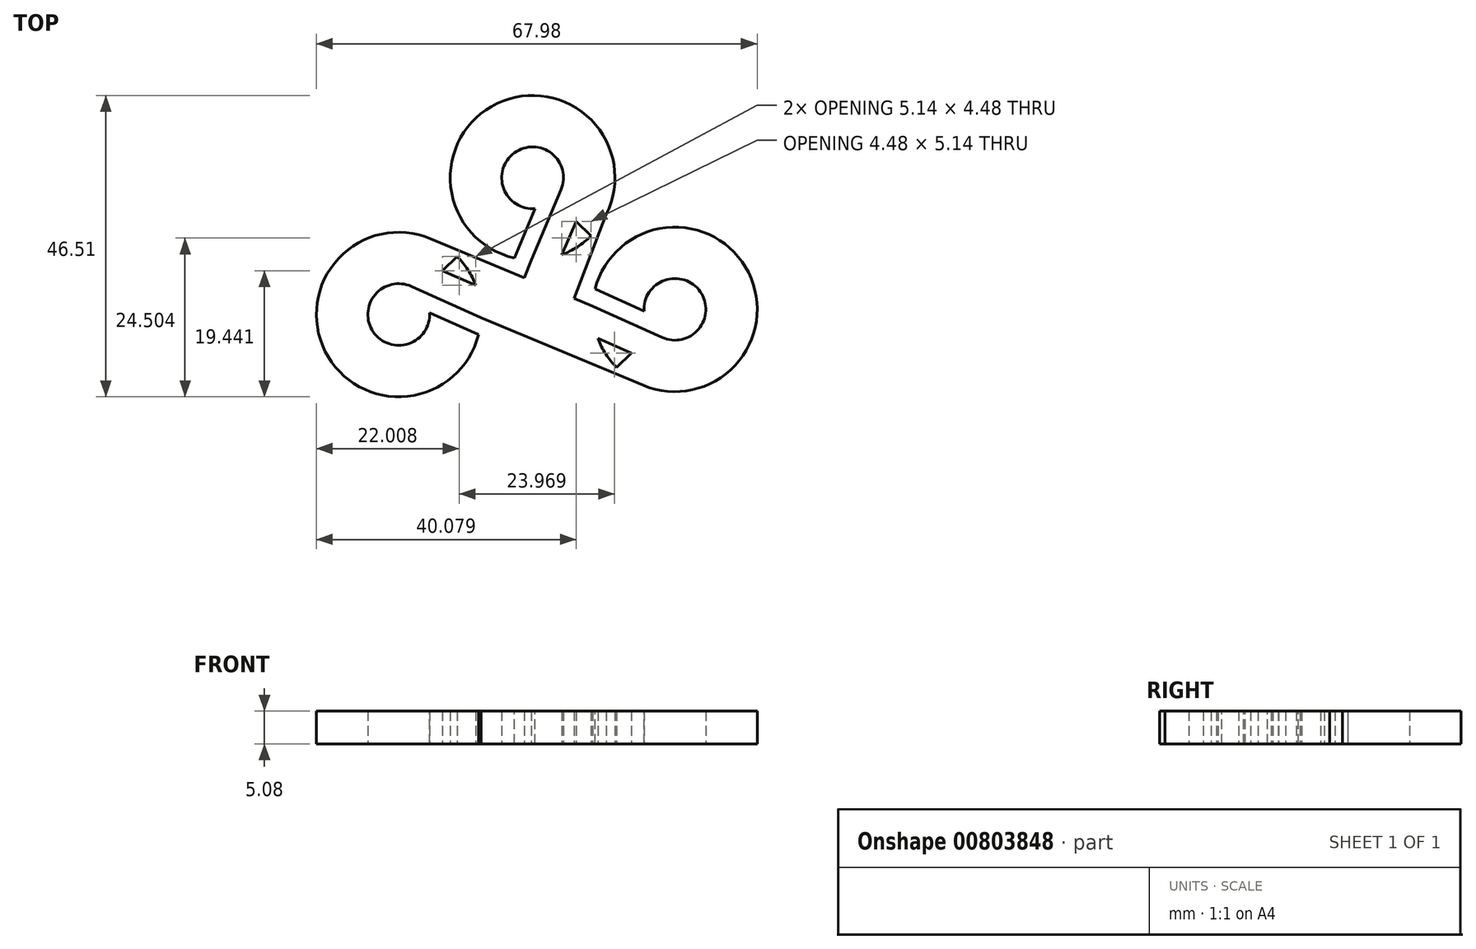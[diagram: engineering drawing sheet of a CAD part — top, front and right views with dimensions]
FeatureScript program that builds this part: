
annotation { "Feature Type Name" : "Feature", "Feature Type Description" : "" }
export const myFeature = defineFeature(function(context is Context, id is Id, definition is map)
    precondition{}
    {
        {
            var Q0;
            Q0=qCreatedBy(makeId("Top.planeOp"),FACE);
            var sketch = newSketch(context, id + "F0", { "sketchPlane" : qUnion([Q0])});
            skCircle(sketch, "E0", {"center": v(0, 0) * mm, "radius": 12.7 * mm});
            skCircle(sketch, "E1", {"center": v(21.94, -20.3) * mm, "radius": 12.7 * mm});
            skCircle(sketch, "E2", {"center": v(-20.64, -21.1) * mm, "radius": 12.7 * mm});
            skLineSegment(sketch, "E3", {"start": v(21.94, -20.3) * mm, "end": v(21.94, -33) * mm});
            skLineSegment(sketch, "E4", {"start": v(0, 0) * mm, "end": v(0, -12.7) * mm});
            skLineSegment(sketch, "E5", {"start": v(0, 0) * mm, "end": v(8.98, -8.98) * mm});
            skLineSegment(sketch, "E6", {"start": v(21.94, -20.3) * mm, "end": v(12.96, -29.29) * mm});
            skCircle(sketch, "E7", {"center": v(21.94, -20.3) * mm, "radius": 4.76 * mm});
            skLineSegment(sketch, "E8", {"start": v(21.94, -20.3) * mm, "end": v(17.45, -24.8) * mm});
            skCircle(sketch, "E9", {"center": v(0, 0) * mm, "radius": 4.76 * mm});
            skLineSegment(sketch, "E10", {"start": v(0, 0) * mm, "end": v(4.5, -4.5) * mm});
            skLineSegment(sketch, "E11", {"start": v(-20.64, -21.1) * mm, "end": v(-11.66, -12.13) * mm});
            skCircle(sketch, "E12", {"center": v(-20.64, -21.1) * mm, "radius": 4.76 * mm});
            skLineSegment(sketch, "E13", {"start": v(-20.64, -21.1) * mm, "end": v(-7.94, -21.1) * mm});
            skLineSegment(sketch, "E14", {"start": v(17.45, -24.8) * mm, "end": v(12.96, -29.29) * mm});
            skLineSegment(sketch, "E15", {"start": v(12.96, -29.29) * mm, "end": v(15.2, -27.04) * mm});
            skLineSegment(sketch, "E16", {"start": v(4.5, -4.5) * mm, "end": v(8.98, -8.98) * mm});
            skLineSegment(sketch, "E17", {"start": v(-16.15, -16.62) * mm, "end": v(-11.66, -12.13) * mm});
            skLineSegment(sketch, "E18", {"start": v(-17.27, -17.74) * mm, "end": v(17.06, -32.03) * mm});
            skLineSegment(sketch, "E19", {"start": v(18.58, -23.68) * mm, "end": v(-15.76, -9.38) * mm});
            skLineSegment(sketch, "E20", {"start": v(3.37, -3.37) * mm, "end": v(-1.24, -15.43) * mm});
            skLineSegment(sketch, "E21", {"start": v(-17.27, -17.74) * mm, "end": v(-13.9, -14.37) * mm});
            skLineSegment(sketch, "E22", {"start": v(-13.9, -14.37) * mm, "end": v(15.2, -27.04) * mm});
            skLineSegment(sketch, "E23", {"start": v(6.74, -6.74) * mm, "end": v(0.65, -20.7) * mm});
            skLineSegment(sketch, "E24", {"start": v(11.39, -5.62) * mm, "end": v(6.42, -18.62) * mm});
            skSolve(sketch);
        }
        {
            var Q0;
            Q0=qSketchRegion(id+"F0",true);
            var Q1;
            {var subQ0=sQuery(id+"F0.wireOp",EDGE,"yDXB3k3o-TFvE-FYoA-wN1f-QkH4QK7AQUMg");var subQ1=sQuery(id+"F0.wireOp",EDGE,"E0");var subQ2=makeQuery(id+"F0.imprint","INTERSECT",VERTEX,{"derivedFrom":[subQ1,subQ0]});Q1=makeQuery(id+"F0.imprint","IMPRINT",FACE,{"disambiguationData":[TD([[makeQuery(id+"F0.imprint","IMPRINT",EDGE,{"disambiguationData":[TD([[subQ2,-1.0]])],"derivedFrom":subQ1}),1.0]])]});}
            var Q2;
            {var subQ0=sQuery(id+"F0.wireOp",EDGE,"E17");var subQ3=sQuery(id+"F0.wireOp",EDGE,"J90078Zz-WnI3-3mMf-xPuW-VheWCmXxd4jc");var subQ5=makeQuery(id+"F0.imprint","INTERSECT",VERTEX,{"derivedFrom":[subQ0,subQ3]});Q2=makeQuery(id+"F0.imprint","IMPRINT",FACE,{"disambiguationData":[TD([[makeQuery(id+"F0.imprint","IMPRINT",EDGE,{"disambiguationData":[TD([[subQ5,-1.0]])],"derivedFrom":subQ3}),1.0]])]});}
            var Q3;
            {var subQ0=sQuery(id+"F0.wireOp",EDGE,"E16");var subQ3=sQuery(id+"F0.wireOp",EDGE,"qBhyJChg-6HFi-ImKc-3mO0-xAAPeeJnZw3U");var subQ5=makeQuery(id+"F0.imprint","INTERSECT",VERTEX,{"derivedFrom":[subQ0,subQ3]});Q3=makeQuery(id+"F0.imprint","IMPRINT",FACE,{"disambiguationData":[TD([[makeQuery(id+"F0.imprint","IMPRINT",EDGE,{"disambiguationData":[TD([[subQ5,-1.0]])],"derivedFrom":subQ3}),1.0]])]});}
            var Q4;
            {var subQ0=sQuery(id+"F0.wireOp",EDGE,"E15");Q4=makeQuery(id+"F0.imprint","IMPRINT",FACE,{"disambiguationData":[TD([[makeQuery(id+"F0.imprint","IMPRINT",EDGE,{"derivedFrom":subQ0}),1.0]])]});}
            var Q5;
            {var subQ0=sQuery(id+"F0.wireOp",EDGE,"uzKKBWqX-qUkN-Bwqt-uPOb-Zz89Ibqqk1gW");var subQ1=sQuery(id+"F0.wireOp",EDGE,"E2");var subQ2=makeQuery(id+"F0.imprint","INTERSECT",VERTEX,{"derivedFrom":[subQ1,subQ0]});Q5=makeQuery(id+"F0.imprint","IMPRINT",FACE,{"disambiguationData":[TD([[makeQuery(id+"F0.imprint","IMPRINT",EDGE,{"disambiguationData":[TD([[subQ2,-1.0]])],"derivedFrom":subQ1}),-1.0]])]});}
            var Q6;
            {var subQ0=sQuery(id+"F0.wireOp",EDGE,"bYxaBZOP-HbRW-pdFW-15Ub-mmeAeTIA2QFz");Q6=makeQuery(id+"F0.imprint","IMPRINT",FACE,{"disambiguationData":[TD([[makeQuery(id+"F0.imprint","IMPRINT",EDGE,{"derivedFrom":subQ0}),-1.0]])]});}
            var Q7;
            {var subQ0=sQuery(id+"F0.wireOp",EDGE,"uzKKBWqX-qUkN-Bwqt-uPOb-Zz89Ibqqk1gW");var subQ1=sQuery(id+"F0.wireOp",EDGE,"E2");var subQ2=makeQuery(id+"F0.imprint","INTERSECT",VERTEX,{"derivedFrom":[subQ1,subQ0]});Q7=makeQuery(id+"F0.imprint","IMPRINT",FACE,{"disambiguationData":[TD([[makeQuery(id+"F0.imprint","IMPRINT",EDGE,{"disambiguationData":[TD([[subQ2,-1.0]])],"derivedFrom":subQ1}),1.0]])]});}
            var Q8;
            {var subQ0=sQuery(id+"F0.wireOp",EDGE,"Z3ejKgqz-Hqn6-uIZ8-Rk3e-6zc6qRlB8dJ0");Q8=makeQuery(id+"F0.imprint","IMPRINT",FACE,{"disambiguationData":[TD([[makeQuery(id+"F0.imprint","IMPRINT",EDGE,{"derivedFrom":subQ0}),-1.0]])]});}
            var Q9;
            {var subQ1=sQuery(id+"F0.wireOp",EDGE,"E0");var subQ3=sQuery(id+"F0.wireOp",EDGE,"qBhyJChg-6HFi-ImKc-3mO0-xAAPeeJnZw3U");var subQ4=makeQuery(id+"F0.imprint","INTERSECT",VERTEX,{"derivedFrom":[subQ1,subQ3]});Q9=makeQuery(id+"F0.imprint","IMPRINT",FACE,{"disambiguationData":[TD([[makeQuery(id+"F0.imprint","IMPRINT",EDGE,{"disambiguationData":[TD([[subQ4,-1.0]])],"derivedFrom":subQ3}),1.0]])]});}
            var Q10;
            {var subQ3=sQuery(id+"F0.wireOp",EDGE,"E0");var subQ5=sQuery(id+"F0.wireOp",EDGE,"E4");var subQ6=makeQuery(id+"F0.imprint","INTERSECT",VERTEX,{"derivedFrom":[subQ3,subQ5]});Q10=makeQuery(id+"F0.imprint","IMPRINT",FACE,{"disambiguationData":[TD([[makeQuery(id+"F0.imprint","IMPRINT",EDGE,{"disambiguationData":[TD([[subQ6,-1.0]])],"derivedFrom":subQ3}),1.0]])]});}
            var Q11;
            {var subQ0=sQuery(id+"F0.wireOp",EDGE,"yDXB3k3o-TFvE-FYoA-wN1f-QkH4QK7AQUMg");var subQ1=sQuery(id+"F0.wireOp",EDGE,"E0");var subQ2=makeQuery(id+"F0.imprint","INTERSECT",VERTEX,{"derivedFrom":[subQ1,subQ0]});Q11=makeQuery(id+"F0.imprint","IMPRINT",FACE,{"disambiguationData":[TD([[makeQuery(id+"F0.imprint","IMPRINT",EDGE,{"disambiguationData":[TD([[subQ2,-1.0]])],"derivedFrom":subQ1}),-1.0]])]});}
            var Q12;
            {var subQ0=sQuery(id+"F0.wireOp",EDGE,"Z3ejKgqz-Hqn6-uIZ8-Rk3e-6zc6qRlB8dJ0");Q12=makeQuery(id+"F0.imprint","IMPRINT",FACE,{"disambiguationData":[TD([[makeQuery(id+"F0.imprint","IMPRINT",EDGE,{"derivedFrom":subQ0}),1.0]])]});}
            var Q13;
            {var subQ0=sQuery(id+"F0.wireOp",EDGE,"6yfvUeka-AtBQ-0gim-mu1m-la48lc1LBtnG");var subQ5=sQuery(id+"F0.wireOp",EDGE,"qBhyJChg-6HFi-ImKc-3mO0-xAAPeeJnZw3U");var subQ6=makeQuery(id+"F0.imprint","INTERSECT",VERTEX,{"derivedFrom":[subQ0,subQ5]});Q13=makeQuery(id+"F0.imprint","IMPRINT",FACE,{"disambiguationData":[TD([[makeQuery(id+"F0.imprint","IMPRINT",EDGE,{"disambiguationData":[TD([[subQ6,1.0]])],"derivedFrom":subQ5}),-1.0]])]});}
            var Q14;
            {var subQ0=sQuery(id+"F0.wireOp",EDGE,"6yfvUeka-AtBQ-0gim-mu1m-la48lc1LBtnG");var subQ5=sQuery(id+"F0.wireOp",EDGE,"qBhyJChg-6HFi-ImKc-3mO0-xAAPeeJnZw3U");var subQ6=makeQuery(id+"F0.imprint","INTERSECT",VERTEX,{"derivedFrom":[subQ0,subQ5]});Q14=makeQuery(id+"F0.imprint","IMPRINT",FACE,{"disambiguationData":[TD([[makeQuery(id+"F0.imprint","IMPRINT",EDGE,{"disambiguationData":[TD([[subQ6,1.0]])],"derivedFrom":subQ5}),1.0]])]});}
            var Q15;
            {var subQ0=sQuery(id+"F0.wireOp",EDGE,"z5MUbxWM-Vo3r-AQEv-g91w-RWlkdqbgf4P1");Q15=makeQuery(id+"F0.imprint","IMPRINT",FACE,{"disambiguationData":[TD([[makeQuery(id+"F0.imprint","IMPRINT",EDGE,{"derivedFrom":subQ0}),-1.0]])]});}
            var Q16;
            {var subQ1=sQuery(id+"F0.wireOp",EDGE,"E12");var subQ3=sQuery(id+"F0.wireOp",EDGE,"E13");var subQ4=makeQuery(id+"F0.imprint","INTERSECT",VERTEX,{"derivedFrom":[subQ1,subQ3]});Q16=makeQuery(id+"F0.imprint","IMPRINT",FACE,{"disambiguationData":[TD([[makeQuery(id+"F0.imprint","IMPRINT",EDGE,{"disambiguationData":[TD([[subQ4,-1.0]])],"derivedFrom":subQ3}),1.0]])]});}
            var Q17;
            {var subQ3=sQuery(id+"F0.wireOp",EDGE,"E2");var subQ7=sQuery(id+"F0.wireOp",EDGE,"E13");var subQ8=makeQuery(id+"F0.imprint","INTERSECT",VERTEX,{"derivedFrom":[subQ3,subQ7]});Q17=makeQuery(id+"F0.imprint","IMPRINT",FACE,{"disambiguationData":[TD([[makeQuery(id+"F0.imprint","IMPRINT",EDGE,{"disambiguationData":[TD([[subQ8,-1.0]])],"derivedFrom":subQ3}),1.0]])]});}
            var Q18;
            {var subQ5=sQuery(id+"F0.wireOp",EDGE,"E14");Q18=makeQuery(id+"F0.imprint","IMPRINT",FACE,{"disambiguationData":[TD([[makeQuery(id+"F0.imprint","IMPRINT",EDGE,{"derivedFrom":subQ5}),-1.0]])]});}
            var Q19;
            {var subQ0=sQuery(id+"F0.wireOp",EDGE,"NG6Fn4Pl-cfwn-nJXz-Nv7R-ltP6G86gKaW2");var subQ1=sQuery(id+"F0.wireOp",EDGE,"E1");var subQ2=makeQuery(id+"F0.imprint","INTERSECT",VERTEX,{"derivedFrom":[subQ1,subQ0]});Q19=makeQuery(id+"F0.imprint","IMPRINT",FACE,{"disambiguationData":[TD([[makeQuery(id+"F0.imprint","IMPRINT",EDGE,{"disambiguationData":[TD([[subQ2,-1.0]])],"derivedFrom":subQ1}),-1.0]])]});}
            var Q20;
            {var subQ0=sQuery(id+"F0.wireOp",EDGE,"bYxaBZOP-HbRW-pdFW-15Ub-mmeAeTIA2QFz");Q20=makeQuery(id+"F0.imprint","IMPRINT",FACE,{"disambiguationData":[TD([[makeQuery(id+"F0.imprint","IMPRINT",EDGE,{"derivedFrom":subQ0}),1.0]])]});}
            var Q21;
            {var subQ1=sQuery(id+"F0.wireOp",EDGE,"z5MUbxWM-Vo3r-AQEv-g91w-RWlkdqbgf4P1");Q21=makeQuery(id+"F0.imprint","IMPRINT",FACE,{"disambiguationData":[TD([[makeQuery(id+"F0.imprint","IMPRINT",EDGE,{"derivedFrom":subQ1}),1.0]])]});}
            var Q22;
            {var subQ0=sQuery(id+"F0.wireOp",EDGE,"eJoCJf4v-nHHx-lm19-L27D-6VjAbPNY3byg");var subQ1=sQuery(id+"F0.wireOp",EDGE,"E2");var subQ2=makeQuery(id+"F0.imprint","INTERSECT",VERTEX,{"derivedFrom":[subQ1,subQ0]});Q22=makeQuery(id+"F0.imprint","IMPRINT",FACE,{"disambiguationData":[TD([[makeQuery(id+"F0.imprint","IMPRINT",EDGE,{"disambiguationData":[TD([[subQ2,-1.0]])],"derivedFrom":subQ1}),1.0]])]});}
            var Q23;
            {var subQ0=sQuery(id+"F0.wireOp",EDGE,"E9");var subQ1=sQuery(id+"F0.wireOp",EDGE,"E4");var subQ2=makeQuery(id+"F0.imprint","INTERSECT",VERTEX,{"derivedFrom":[subQ1,subQ0]});Q23=makeQuery(id+"F0.imprint","IMPRINT",FACE,{"disambiguationData":[TD([[makeQuery(id+"F0.imprint","IMPRINT",EDGE,{"disambiguationData":[TD([[subQ2,-1.0]])],"derivedFrom":subQ1}),1.0]])]});}
            var Q24;
            {var subQ0=sQuery(id+"F0.wireOp",EDGE,"E17");Q24=makeQuery(id+"F0.imprint","IMPRINT",FACE,{"disambiguationData":[TD([[makeQuery(id+"F0.imprint","IMPRINT",EDGE,{"derivedFrom":subQ0}),-1.0]])]});}
            var Q25;
            {var subQ0=sQuery(id+"F0.wireOp",EDGE,"E16");var subQ1=sQuery(id+"F0.wireOp",EDGE,"E0");var subQ2=makeQuery(id+"F0.imprint","INTERSECT",VERTEX,{"derivedFrom":[subQ1,subQ0]});Q25=makeQuery(id+"F0.imprint","IMPRINT",FACE,{"disambiguationData":[TD([[makeQuery(id+"F0.imprint","IMPRINT",EDGE,{"disambiguationData":[TD([[subQ2,1.0]])],"derivedFrom":subQ1}),1.0]])]});}
            extrude(context, id + "F1", {"entities" : qUnion([Q0, Q1, Q2, Q3, Q4, Q5, Q6, Q7, Q8, Q9, Q10, Q11, Q12, Q13, Q14, Q15, Q16, Q17, Q18, Q19, Q20, Q21, Q22, Q23, Q24, Q25]), "depth" : 5.08 * mm, "offsetDistance" : 25.4 * mm});
        }
        {
            var Q0;
            Q0=makeQuery(id+"F1.opExtrude","CAP_FACE",FACE,{"disambiguationData":[OSD([sQuery(id+"F0.wireOp",EDGE,"E0"),sQuery(id+"F0.wireOp",EDGE,"E1"),sQuery(id+"F0.wireOp",EDGE,"E2"),sQuery(id+"F0.wireOp",EDGE,"VeAweMac-LZ9O-rFIa-PTyz-U5xl3IZNd5pn"),sQuery(id+"F0.wireOp",EDGE,"E7"),sQuery(id+"F0.wireOp",EDGE,"NG6Fn4Pl-cfwn-nJXz-Nv7R-ltP6G86gKaW2"),sQuery(id+"F0.wireOp",EDGE,"E9"),sQuery(id+"F0.wireOp",EDGE,"yDXB3k3o-TFvE-FYoA-wN1f-QkH4QK7AQUMg"),sQuery(id+"F0.wireOp",EDGE,"6yfvUeka-AtBQ-0gim-mu1m-la48lc1LBtnG"),sQuery(id+"F0.wireOp",EDGE,"E12"),sQuery(id+"F0.wireOp",EDGE,"uzKKBWqX-qUkN-Bwqt-uPOb-Zz89Ibqqk1gW"),sQuery(id+"F0.wireOp",EDGE,"z5MUbxWM-Vo3r-AQEv-g91w-RWlkdqbgf4P1"),sQuery(id+"F0.wireOp",EDGE,"qBhyJChg-6HFi-ImKc-3mO0-xAAPeeJnZw3U"),sQuery(id+"F0.wireOp",EDGE,"Vy6klFHD-ql6F-NG0b-UYJ5-acndccB01QWS"),sQuery(id+"F0.wireOp",EDGE,"OdPr5M7K-QP7o-Xsb9-YXNN-OMWYOfSv6xGX"),sQuery(id+"F0.wireOp",EDGE,"tfzjCEgK-RNZ7-z4IH-43NG-UBwa0SwhfyJe")])],"isStart":false});
            var sketch = newSketch(context, id + "F2", { "sketchPlane" : qUnion([Q0])});
            skLineSegment(sketch, "E25", {"start": v(-0.2, -12.7) * mm, "end": v(4.39, -1.86) * mm});
            skLineSegment(sketch, "E26", {"start": v(-2.82, -12.38) * mm, "end": v(0.4, -4.75) * mm});
            skLineSegment(sketch, "E27", {"start": v(-7.95, -21.62) * mm, "end": v(-18.68, -16.77) * mm});
            skLineSegment(sketch, "E28", {"start": v(-15.88, -20.82) * mm, "end": v(-8.33, -24.24) * mm});
            skLineSegment(sketch, "E29", {"start": v(9.25, -19.8) * mm, "end": v(19.98, -24.65) * mm});
            skLineSegment(sketch, "E30", {"start": v(9.63, -17.18) * mm, "end": v(17.19, -20.6) * mm});
            skSolve(sketch);
        }
        {
            var Q0;
            {var subQ0=sQuery(id+"F2.wireOp",EDGE,"E27");Q0=makeQuery(id+"F2.imprint","IMPRINT",FACE,{"disambiguationData":[TD([[makeQuery(id+"F2.imprint","IMPRINT",EDGE,{"derivedFrom":subQ0}),1.0]])]});}
            var Q1;
            {var subQ0=sQuery(id+"F2.wireOp",EDGE,"E25");Q1=makeQuery(id+"F2.imprint","IMPRINT",FACE,{"disambiguationData":[TD([[makeQuery(id+"F2.imprint","IMPRINT",EDGE,{"derivedFrom":subQ0}),1.0]])]});}
            var Q2;
            {var subQ0=sQuery(id+"F2.wireOp",EDGE,"E29");Q2=makeQuery(id+"F2.imprint","IMPRINT",FACE,{"disambiguationData":[TD([[makeQuery(id+"F2.imprint","IMPRINT",EDGE,{"derivedFrom":subQ0}),1.0]])]});}
            extrude(context, id + "F3", {"entities" : qUnion([Q0, Q1, Q2]), "operationType" : NewBodyOperationType.REMOVE, "oppositeDirection" : true, "depth" : 25.4 * mm, "offsetDistance" : 25.4 * mm});
        }
    });
